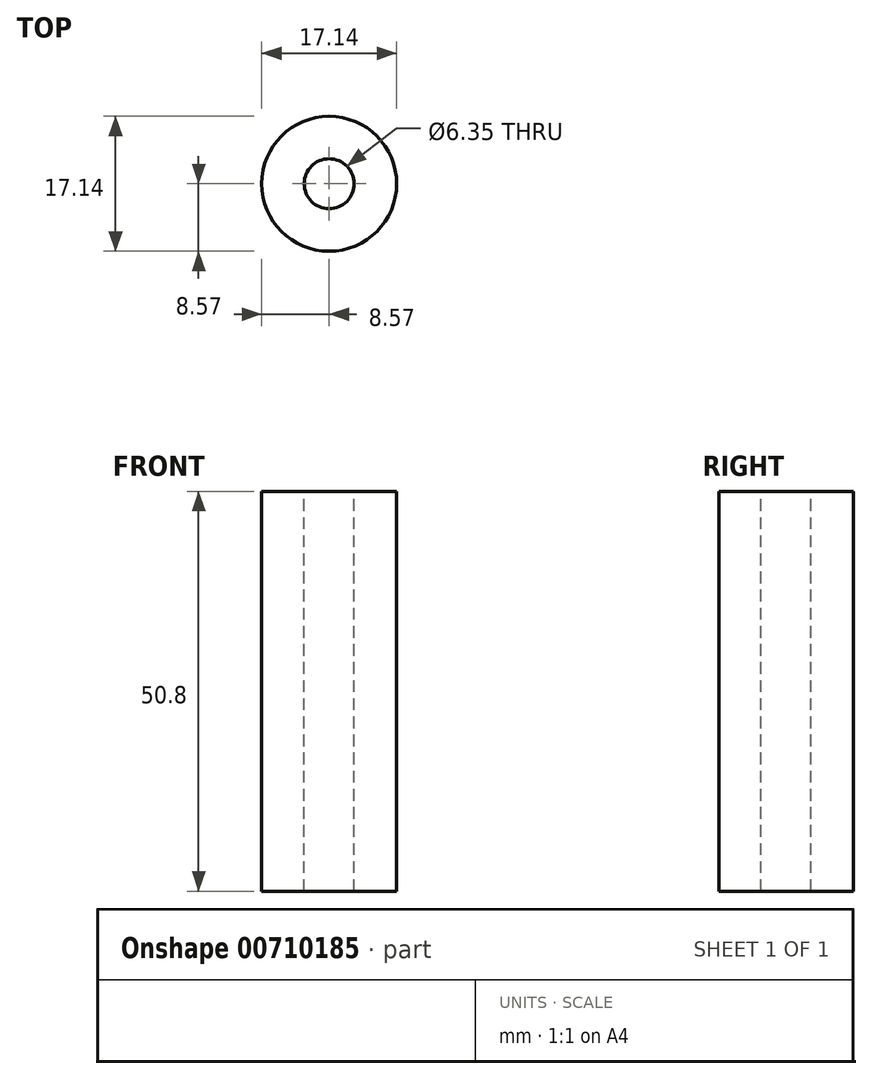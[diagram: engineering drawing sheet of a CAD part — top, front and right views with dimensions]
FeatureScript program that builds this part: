
annotation { "Feature Type Name" : "Feature", "Feature Type Description" : "" }
export const myFeature = defineFeature(function(context is Context, id is Id, definition is map)
    precondition{}
    {
        {
            var Q0;
            Q0=qCreatedBy(makeId("Top.planeOp"),FACE);
            var sketch = newSketch(context, id + "F0", { "sketchPlane" : qUnion([Q0])});
            skCircle(sketch, "E0", {"center": v(0, 0) * mm, "radius": 8.57 * mm});
            skSolve(sketch);
        }
        {
            var Q0;
            Q0=makeQuery(id+"F0.imprint","IMPRINT",FACE,{"disambiguationData":[TD([[makeQuery(id+"F0.imprint","IMPRINT",EDGE,{"derivedFrom":sQuery(id+"F0.wireOp",EDGE,"E0")}),1.0]])]});
            extrude(context, id + "F1", {"entities" : qUnion([Q0]), "depth" : 50.8 * mm, "offsetDistance" : 25.4 * mm});
        }
        {
            var Q0;
            Q0=makeQuery(id+"F1.opExtrude","CAP_FACE",FACE,{"disambiguationData":[OSD([sQuery(id+"F0.wireOp",EDGE,"E0")])],"isStart":false});
            var sketch = newSketch(context, id + "F2", { "sketchPlane" : qUnion([Q0])});
            skSolve(sketch);
        }
        {
            var Q0;
            Q0=makeQuery(id+"F2.imprint","IMPRINT",FACE,{"disambiguationData":[TD([[makeQuery(id+"F2.imprint","IMPRINT",EDGE,{"derivedFrom":makeQuery(id+"F1.opExtrude","CAP_EDGE",EDGE,{"disambiguationData":[OSD([sQuery(id+"F0.wireOp",EDGE,"E0")])],"isStart":false})}),1.0]])]});
            var sketch = newSketch(context, id + "F3", { "sketchPlane" : qUnion([Q0])});
            skCircle(sketch, "E1", {"center": v(0, 0) * mm, "radius": 4.93 * mm});
            skSolve(sketch);
        }
        {
            var Q0;
            Q0=sQuery(id+"F3.wireOp",VERTEX,"E1.center");
            var Q1;
            Q1=makeQuery(id+"F1.opExtrude","SWEPT_BODY",BODY,{"disambiguationData":[OSD([sQuery(id+"F0.wireOp",EDGE,"E0")])]});
            hole(context, id + "F4", {"style" : HoleStyle.SIMPLE, "endStyle" : HoleEndStyle.THROUGH, "holeDiameter" : 6.35 * mm, "majorDiameter" : 6.35 * mm, "isTappedThrough" : true, "tappedDepth" : 12.7 * mm, "tapClearance" : 3, "locations" : qUnion([Q0]), "scope" : qUnion([Q1])});
        }
    });
